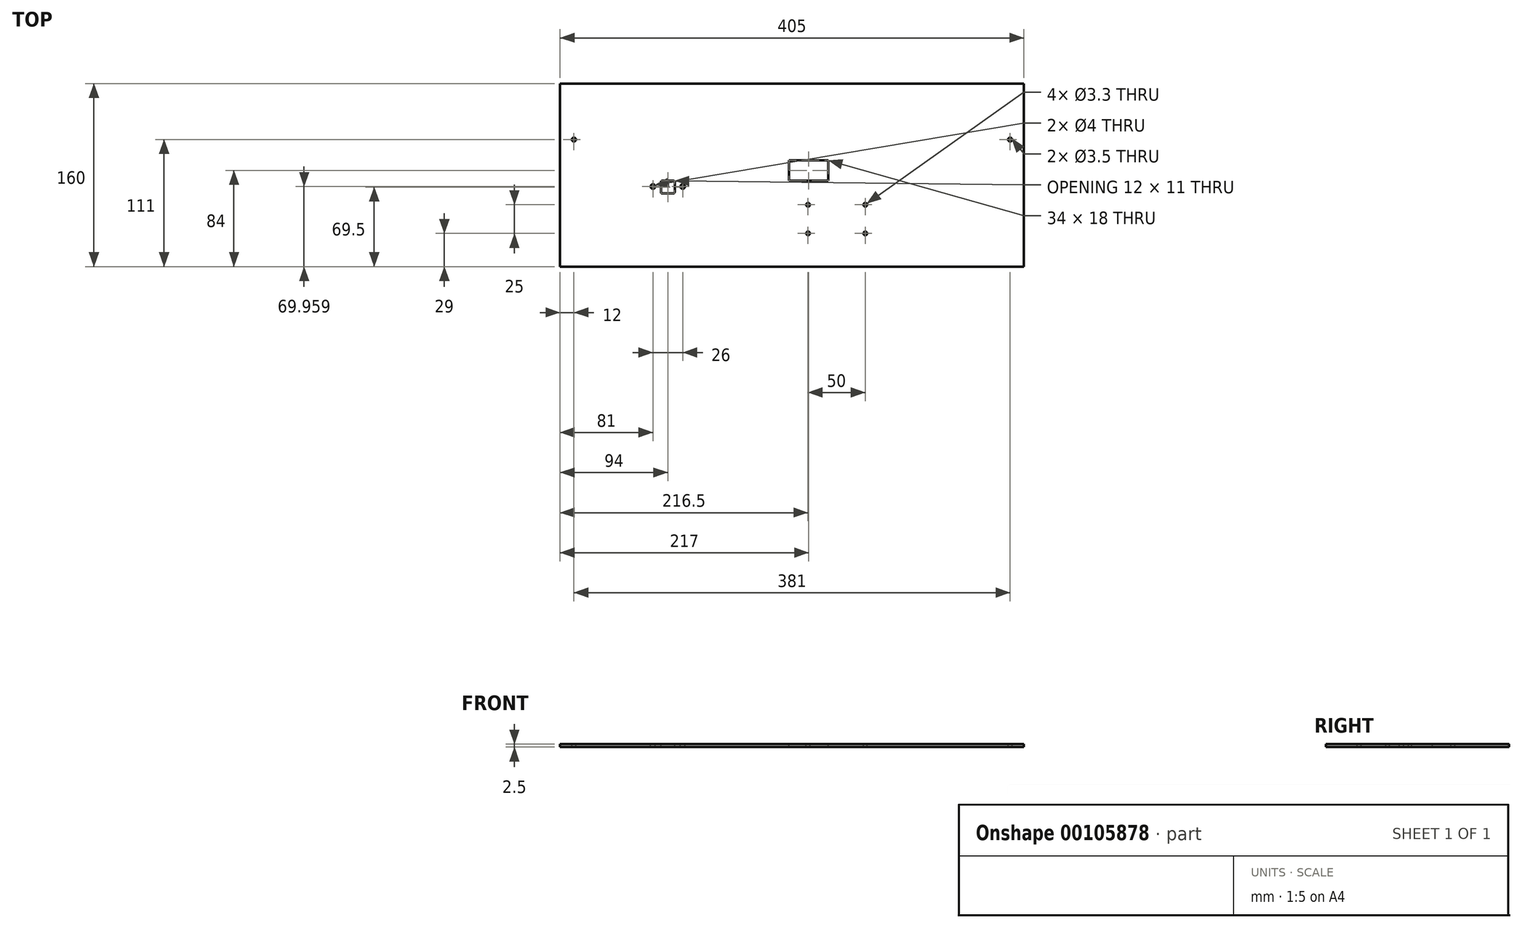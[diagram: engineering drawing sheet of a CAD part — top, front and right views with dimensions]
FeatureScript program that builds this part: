
annotation { "Feature Type Name" : "Feature", "Feature Type Description" : "" }
export const myFeature = defineFeature(function(context is Context, id is Id, definition is map)
    precondition{}
    {
        {
            var Q0;
            Q0=qCreatedBy(makeId("Top.planeOp"),FACE);
            var sketch = newSketch(context, id + "F0", { "sketchPlane" : qUnion([Q0])});
            skLineSegment(sketch, "E0.bottom", {"start": v(0, 0) * mm, "end": v(405, 0) * mm});
            skLineSegment(sketch, "E0.top", {"start": v(0, 160) * mm, "end": v(405, 160) * mm});
            skLineSegment(sketch, "E0.left", {"start": v(0, 0) * mm, "end": v(0, 160) * mm});
            skLineSegment(sketch, "E0.right", {"start": v(405, 0) * mm, "end": v(405, 160) * mm});
            skSolve(sketch);
        }
        {
            var Q0;
            Q0 = qSketchRegion(id + "F0", true);
            extrude(context, id + "F1", {"entities" : qUnion([Q0]), "depth" : 2.5 * mm, "offsetDistance" : 25 * mm});
        }
        {
            var Q0;
            Q0=makeQuery(id+"F1.opExtrude","CAP_FACE",FACE,{"disambiguationData":[OSD([sQuery(id+"F0.wireOp",EDGE,"E0.bottom"),sQuery(id+"F0.wireOp",EDGE,"E0.top"),sQuery(id+"F0.wireOp",EDGE,"E0.left"),sQuery(id+"F0.wireOp",EDGE,"E0.right")])],"isStart":false});
            var sketch = newSketch(context, id + "F2", { "sketchPlane" : qUnion([Q0])});
            skPoint(sketch, "E1", {"position": v(12, 111) * mm});
            skPoint(sketch, "E2", {"position": v(393, 111) * mm});
            skCircle(sketch, "E3", {"center": v(12, 111) * mm, "radius": 1.75 * mm});
            skCircle(sketch, "E4", {"center": v(393, 111) * mm, "radius": 1.75 * mm});
            skSolve(sketch);
        }
        {
            var Q0;
            Q0=makeQuery(id+"F1.opExtrude","CAP_FACE",FACE,{"disambiguationData":[OSD([sQuery(id+"F0.wireOp",EDGE,"E0.bottom"),sQuery(id+"F0.wireOp",EDGE,"E0.top"),sQuery(id+"F0.wireOp",EDGE,"E0.left"),sQuery(id+"F0.wireOp",EDGE,"E0.right")])],"isStart":false});
            var sketch = newSketch(context, id + "F3", { "sketchPlane" : qUnion([Q0])});
            skLineSegment(sketch, "E5.bottom", {"start": v(89, 75) * mm, "end": v(99, 75) * mm});
            skLineSegment(sketch, "E5.top", {"start": v(89, 64) * mm, "end": v(99, 64) * mm});
            skLineSegment(sketch, "E5.left", {"start": v(88, 74) * mm, "end": v(88, 65) * mm});
            skLineSegment(sketch, "E5.right", {"start": v(100, 74) * mm, "end": v(100, 65) * mm});
            skPoint(sketch, "E6.visualSharp", {"position": v(88, 75) * mm});
            skArc(sketch, "E6.filletArc", {"start": v(89, 75) * mm, "mid": v(88.3, 74.7) * mm, "end": v(88, 74) * mm});
            skPoint(sketch, "E7.visualSharp", {"position": v(100, 75) * mm});
            skArc(sketch, "E7.filletArc", {"start": v(100, 74) * mm, "mid": v(99.7, 74.7) * mm, "end": v(99, 75) * mm});
            skPoint(sketch, "E8.visualSharp", {"position": v(100, 64) * mm});
            skArc(sketch, "E8.filletArc", {"start": v(99, 64) * mm, "mid": v(99.7, 64.3) * mm, "end": v(100, 65) * mm});
            skPoint(sketch, "E9.visualSharp", {"position": v(88, 64) * mm});
            skArc(sketch, "E9.filletArc", {"start": v(88, 65) * mm, "mid": v(88.3, 64.3) * mm, "end": v(89, 64) * mm});
            skCircle(sketch, "E10", {"center": v(81, 69.96) * mm, "radius": 2 * mm});
            skLineSegment(sketch, "E11", {"start": v(94, 80.2) * mm, "end": v(94, 58.98) * mm, "construction": true});
            skPoint(sketch, "E11.startSnap0", {"position": v(94, 75) * mm});
            skCircle(sketch, "E12.MirrorC", {"center": v(107, 69.96) * mm, "radius": 2 * mm});
            skSolve(sketch);
        }
        {
            var Q0;
            Q0 = qSketchRegion(id + "F3", true);
            extrude(context, id + "F4", {"entities" : qUnion([Q0]), "operationType" : NewBodyOperationType.REMOVE, "oppositeDirection" : true, "depth" : 25 * mm});
        }
        {
            var Q0;
            Q0=makeQuery(id+"F1.opExtrude","CAP_FACE",FACE,{"disambiguationData":[OSD([sQuery(id+"F0.wireOp",EDGE,"E0.bottom"),sQuery(id+"F0.wireOp",EDGE,"E0.top"),sQuery(id+"F0.wireOp",EDGE,"E0.left"),sQuery(id+"F0.wireOp",EDGE,"E0.right")])],"isStart":false});
            var sketch = newSketch(context, id + "F5", { "sketchPlane" : qUnion([Q0])});
            skLineSegment(sketch, "E13.bottom", {"start": v(200, 93) * mm, "end": v(234, 93) * mm});
            skLineSegment(sketch, "E13.top", {"start": v(200, 75) * mm, "end": v(234, 75) * mm});
            skLineSegment(sketch, "E13.left", {"start": v(200, 93) * mm, "end": v(200, 75) * mm});
            skLineSegment(sketch, "E13.right", {"start": v(234, 93) * mm, "end": v(234, 75) * mm});
            skLineSegment(sketch, "E14.bottom", {"start": v(194.5, 108.5) * mm, "end": v(288.5, 108.5) * mm, "construction": true});
            skLineSegment(sketch, "E14.top", {"start": v(194.5, 9.5) * mm, "end": v(288.5, 9.5) * mm, "construction": true});
            skLineSegment(sketch, "E14.left", {"start": v(186.5, 100.5) * mm, "end": v(186.5, 17.5) * mm, "construction": true});
            skLineSegment(sketch, "E14.right", {"start": v(296.5, 100.5) * mm, "end": v(296.5, 17.5) * mm, "construction": true});
            skPoint(sketch, "E15.visualSharp", {"position": v(186.5, 108.5) * mm});
            skArc(sketch, "E15.filletArc", {"start": v(194.5, 108.5) * mm, "mid": v(188.84, 106.16) * mm, "end": v(186.5, 100.5) * mm, "construction": true});
            skPoint(sketch, "E16.visualSharp", {"position": v(296.5, 108.5) * mm});
            skArc(sketch, "E16.filletArc", {"start": v(296.5, 100.5) * mm, "mid": v(294.16, 106.16) * mm, "end": v(288.5, 108.5) * mm, "construction": true});
            skPoint(sketch, "E17.visualSharp", {"position": v(296.5, 9.5) * mm});
            skArc(sketch, "E17.filletArc", {"start": v(288.5, 9.5) * mm, "mid": v(294.16, 11.84) * mm, "end": v(296.5, 17.5) * mm, "construction": true});
            skPoint(sketch, "E18.visualSharp", {"position": v(186.5, 9.5) * mm});
            skArc(sketch, "E18.filletArc", {"start": v(186.5, 17.5) * mm, "mid": v(188.84, 11.84) * mm, "end": v(194.5, 9.5) * mm, "construction": true});
            skCircle(sketch, "E19", {"center": v(216.5, 54) * mm, "radius": 1.65 * mm});
            skCircle(sketch, "E20", {"center": v(266.5, 54) * mm, "radius": 1.65 * mm});
            skCircle(sketch, "E21", {"center": v(266.5, 29) * mm, "radius": 1.65 * mm});
            skCircle(sketch, "E22", {"center": v(216.5, 29) * mm, "radius": 1.65 * mm});
            skSolve(sketch);
        }
        {
            var Q0;
            Q0 = qSketchRegion(id + "F5", true);
            extrude(context, id + "F6", {"entities" : qUnion([Q0]), "operationType" : NewBodyOperationType.REMOVE, "oppositeDirection" : true, "depth" : 25 * mm, "offsetDistance" : 25 * mm});
        }
        {
            var Q0;
            Q0 = qSketchRegion(id + "F2", true);
            extrude(context, id + "F7", {"entities" : qUnion([Q0]), "operationType" : NewBodyOperationType.REMOVE, "oppositeDirection" : true, "depth" : 25 * mm, "offsetDistance" : 25 * mm});
        }
    });
